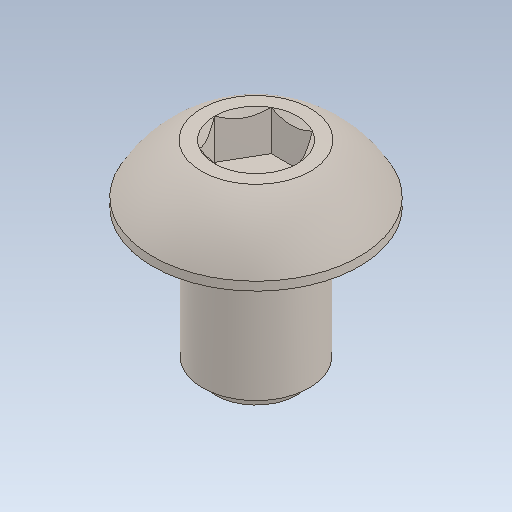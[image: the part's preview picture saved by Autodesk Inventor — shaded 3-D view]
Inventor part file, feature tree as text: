
AUTODESK INVENTOR PART (.ipt)
format: ipt  version: 2020 (Build 240168000, 168)  size: 140,288 bytes
history: native  units: in
note: dims shown in document units (in); Inventor stores cm internally (conversion verified against a paired STEP export)
features: fillet x1
ambient origin geometry x8: Origin, YZ Plane, XZ Plane, XY Plane, X Axis, Y Axis, Z Axis, Center Point
bodies: Solid1 (feature_tree)
feature tree (1):
  fillet  "Fillet1"  [1 undecoded]
note: 1 required parameter value undecoded (feature->parameter linkage not recoverable at this tier; creation-order binding heuristic only, values carry confidence <= 0.55)
